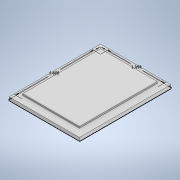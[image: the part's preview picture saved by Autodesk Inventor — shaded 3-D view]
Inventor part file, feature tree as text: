
AUTODESK INVENTOR PART (.ipt)
format: ipt  version: 2020 (Build 240168000, 168)  size: 105,472 bytes
history: native  units: in
note: dims shown in document units (in); Inventor stores cm internally (conversion verified against a paired STEP export)
features: extrude x2, sketch x1
ambient origin geometry x8: Origin, YZ Plane, XZ Plane, XY Plane, X Axis, Y Axis, Z Axis, Center Point
bodies: Solid1 (feature_tree)
feature tree (3):
  sketch  "Sketch1"  dims[d0=1.475in d1=1.915in d2=1.192in d3=1.632in d4=0.1in d5=0.0in d6=0.07in d7=0.0in]
  extrude  "Extrusion1"  Depth=1.915in
  extrude  "Extrusion2"  Depth=1.192in
